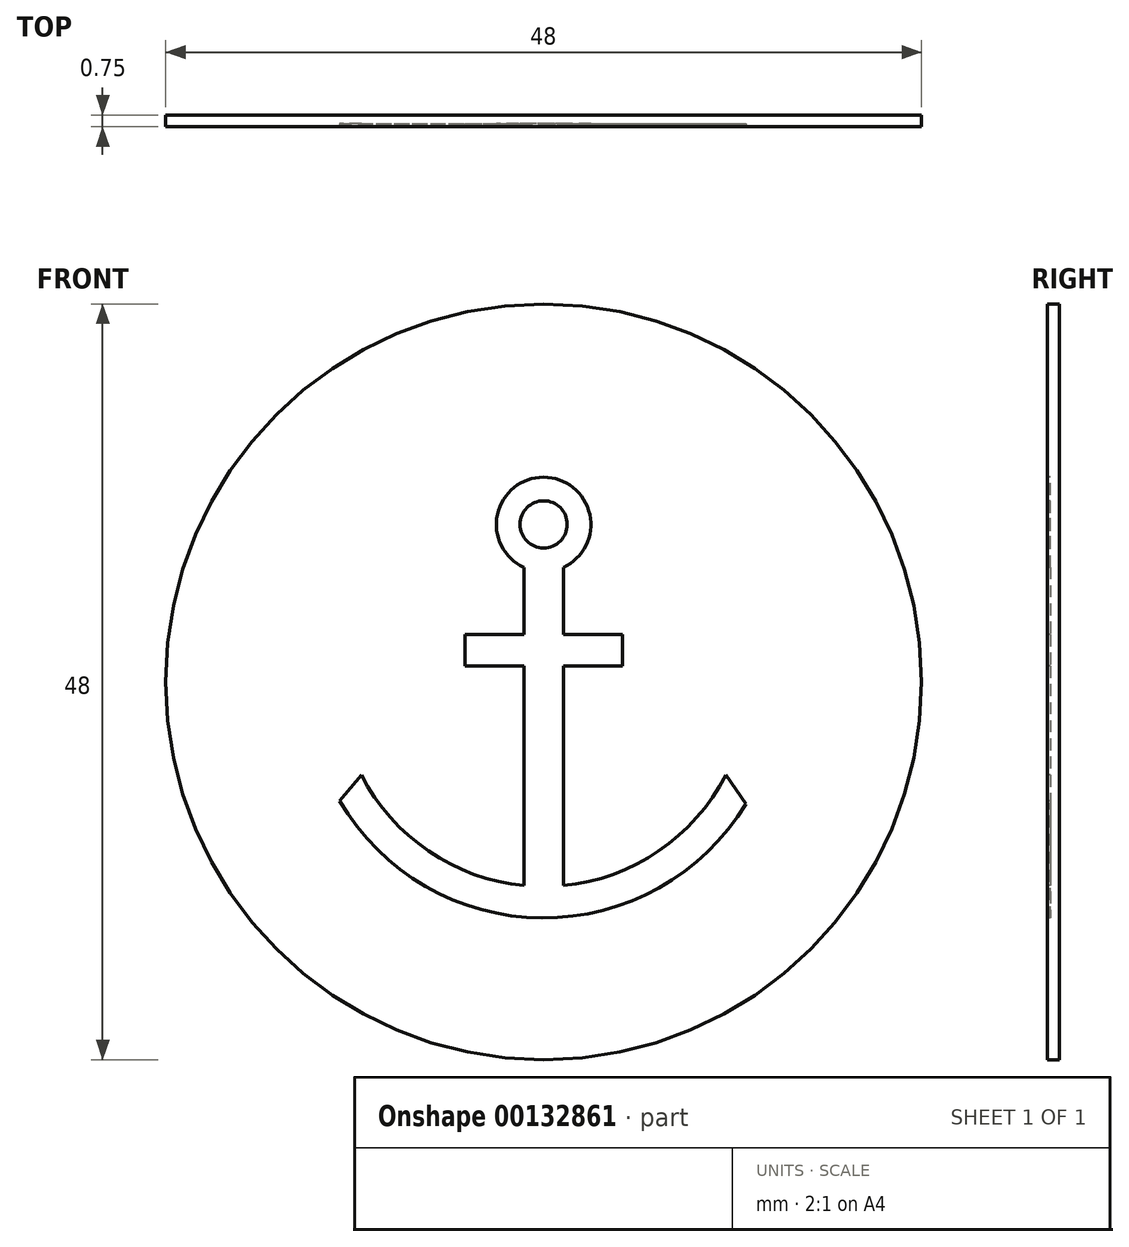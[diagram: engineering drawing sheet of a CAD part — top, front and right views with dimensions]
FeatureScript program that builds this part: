
annotation { "Feature Type Name" : "Feature", "Feature Type Description" : "" }
export const myFeature = defineFeature(function(context is Context, id is Id, definition is map)
    precondition{}
    {
        {
            var Q0;
            Q0=qCreatedBy(makeId("Front.planeOp"),FACE);
            var sketch = newSketch(context, id + "F0", { "sketchPlane" : qUnion([Q0])});
            skCircle(sketch, "E0", {"center": v(0, 0) * mm, "radius": 24 * mm});
            skSolve(sketch);
        }
        {
            var Q0;
            Q0 = qSketchRegion(id + "F0", true);
            extrude(context, id + "F1", {"entities" : qUnion([Q0]), "depth" : 0.75 * mm, "offsetDistance" : 25 * mm});
        }
        {
            var Q0;
            Q0=makeQuery(id+"F1.opExtrude","CAP_FACE",FACE,{"disambiguationData":[OSD([sQuery(id+"F0.wireOp",EDGE,"E0")])],"isStart":false});
            var sketch = newSketch(context, id + "F2", { "sketchPlane" : qUnion([Q0])});
            skArc(sketch, "E1", {"start": v(-12.95, -7.57) * mm, "mid": v(-0.1, -15) * mm, "end": v(12.84, -7.75) * mm});
            skArc(sketch, "E2", {"start": v(1.25, -12.94) * mm, "mid": v(7.3, -10.75) * mm, "end": v(11.57, -5.93) * mm});
            skCircle(sketch, "E3", {"center": v(0, 10) * mm, "radius": 1.5 * mm});
            skArc(sketch, "E4", {"start": v(1.25, 7.27) * mm, "mid": v(0, 13) * mm, "end": v(-1.25, 7.27) * mm});
            skLineSegment(sketch, "E5.left", {"start": v(-1.25, 7.27) * mm, "end": v(-1.25, 3) * mm});
            skLineSegment(sketch, "E5.right", {"start": v(1.25, 7.27) * mm, "end": v(1.25, 3) * mm});
            skPoint(sketch, "E6.orphan", {"position": v(1.25, -14) * mm});
            skLineSegment(sketch, "E7.trimOffspring", {"start": v(-11.57, -5.93) * mm, "end": v(-12.95, -7.57) * mm});
            skLineSegment(sketch, "E8.trimOffspring", {"start": v(11.57, -5.93) * mm, "end": v(12.84, -7.75) * mm});
            skArc(sketch, "E9.trimOffspring", {"start": v(-11.57, -5.93) * mm, "mid": v(-7.3, -10.75) * mm, "end": v(-1.25, -12.94) * mm});
            skLineSegment(sketch, "E10.bottom", {"start": v(-5, 3) * mm, "end": v(-1.25, 3) * mm});
            skLineSegment(sketch, "E10.top", {"start": v(-5, 1) * mm, "end": v(-1.25, 1) * mm});
            skLineSegment(sketch, "E10.left", {"start": v(-5, 3) * mm, "end": v(-5, 1) * mm});
            skLineSegment(sketch, "E10.right", {"start": v(5, 3) * mm, "end": v(5, 1) * mm});
            skLineSegment(sketch, "E11.trimOffspring", {"start": v(-1.25, 1) * mm, "end": v(-1.25, -12.94) * mm});
            skLineSegment(sketch, "E12.trimOffspring", {"start": v(1.25, 3) * mm, "end": v(5, 3) * mm});
            skLineSegment(sketch, "E13.trimOffspring", {"start": v(1.25, 1) * mm, "end": v(1.25, -12.94) * mm});
            skLineSegment(sketch, "E14.trimOffspring", {"start": v(1.25, 1) * mm, "end": v(5, 1) * mm});
            skSolve(sketch);
        }
        {
            var Q0;
            Q0 = qSketchRegion(id + "F2", true);
            extrude(context, id + "F3", {"entities" : qUnion([Q0]), "operationType" : NewBodyOperationType.REMOVE, "oppositeDirection" : true, "depth" : 0.2 * mm, "offsetDistance" : 25 * mm});
        }
    });
